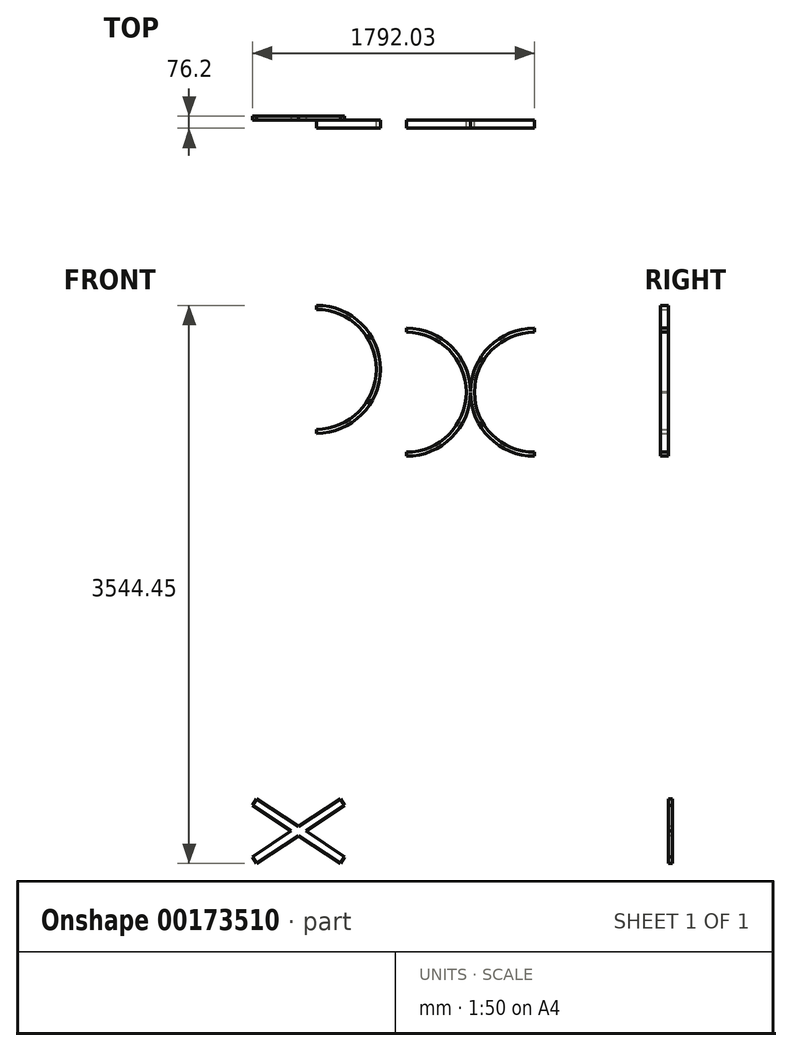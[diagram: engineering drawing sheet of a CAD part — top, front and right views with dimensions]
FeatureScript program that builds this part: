
annotation { "Feature Type Name" : "Feature", "Feature Type Description" : "" }
export const myFeature = defineFeature(function(context is Context, id is Id, definition is map)
    precondition{}
    {
        {
            var Q0;
            Q0=qCreatedBy(makeId("Front.planeOp"),FACE);
            var sketch = newSketch(context, id + "F0", { "sketchPlane" : qUnion([Q0])});
            skLineSegment(sketch, "E0", {"start": v(-517.84, 296.82) * mm, "end": v(548.96, 296.82) * mm, "construction": true});
            skLineSegment(sketch, "E1", {"start": v(15.56, 296.82) * mm, "end": v(15.56, -515.98) * mm, "construction": true});
            skLineSegment(sketch, "E2", {"start": v(421.96, -515.98) * mm, "end": v(904.56, -515.98) * mm});
            skLineSegment(sketch, "E3", {"start": v(904.56, -515.98) * mm, "end": v(421.96, -515.98) * mm});
            skLineSegment(sketch, "E4", {"start": v(15.56, -515.98) * mm, "end": v(15.56, -109.58) * mm, "construction": true});
            skLineSegment(sketch, "E5", {"start": v(15.56, -109.58) * mm, "end": v(-9.84, -109.58) * mm, "construction": true});
            skLineSegment(sketch, "E6", {"start": v(-390.84, 296.84) * mm, "end": v(-390.84, 271.42) * mm});
            skArc(sketch, "E7.MirrorCS", {"start": v(421.96, -515.98) * mm, "mid": v(15.56, -109.58) * mm, "end": v(421.96, 296.82) * mm});
            skLineSegment(sketch, "E8", {"start": v(421.96, 296.82) * mm, "end": v(421.96, 271.42) * mm});
            skArc(sketch, "E9.0", {"start": v(-390.84, -490.58) * mm, "mid": v(-9.84, -109.58) * mm, "end": v(-390.84, 271.42) * mm});
            skArc(sketch, "E10.0", {"start": v(421.96, -490.58) * mm, "mid": v(40.96, -109.58) * mm, "end": v(421.96, 271.42) * mm});
            skLineSegment(sketch, "E11.trimOffspring", {"start": v(-390.84, -490.58) * mm, "end": v(-390.84, -516) * mm});
            skLineSegment(sketch, "E12.trimOffspring", {"start": v(421.96, -490.58) * mm, "end": v(421.96, -515.98) * mm});
            skLineSegment(sketch, "E13.trimOffspring", {"start": v(-390.84, -515.98) * mm, "end": v(-873.44, -515.98) * mm});
            skArc(sketch, "E14.0", {"start": v(-390.84, -516) * mm, "mid": v(-104.6, -398.1) * mm, "end": v(15.57, -112.8) * mm});
            skArc(sketch, "E15.trimOffspring", {"start": v(15.57, -106.37) * mm, "mid": v(-104.6, 178.94) * mm, "end": v(-390.84, 296.84) * mm});
            skLineSegment(sketch, "E16", {"start": v(-390.84, 296.84) * mm, "end": v(421.96, 296.82) * mm});
            skSolve(sketch);
        }
        {
            var Q0;
            {var subQ0=sQuery(id+"F0.wireOp",EDGE,"E6");Q0=makeQuery(id+"F0.imprint","IMPRINT",FACE,{"disambiguationData":[TD([[makeQuery(id+"F0.imprint","IMPRINT",EDGE,{"derivedFrom":subQ0}),1.0]])]});}
            var Q1;
            {var subQ0=sQuery(id+"F0.wireOp",EDGE,"E8");Q1=makeQuery(id+"F0.imprint","IMPRINT",FACE,{"disambiguationData":[TD([[makeQuery(id+"F0.imprint","IMPRINT",EDGE,{"derivedFrom":subQ0}),-1.0]])]});}
            extrude(context, id + "F1", {"entities" : qUnion([Q0, Q1]), "depth" : 50.8 * mm});
        }
        {
            var Q0;
            Q0=qCreatedBy(makeId("Front.planeOp"),FACE);
            var sketch = newSketch(context, id + "F2", { "sketchPlane" : qUnion([Q0])});
            skArc(sketch, "E17", {"start": v(-962.68, -370.57) * mm, "mid": v(-556.28, 35.83) * mm, "end": v(-962.68, 442.23) * mm});
            skLineSegment(sketch, "E18", {"start": v(-962.68, 416.83) * mm, "end": v(-962.68, 442.23) * mm});
            skLineSegment(sketch, "E19", {"start": v(-962.68, 442.23) * mm, "end": v(-962.68, 416.83) * mm});
            skArc(sketch, "E20.0", {"start": v(-962.68, -345.17) * mm, "mid": v(-581.68, 35.83) * mm, "end": v(-962.68, 416.83) * mm});
            skLineSegment(sketch, "E21.trimOffspring", {"start": v(-962.68, -345.17) * mm, "end": v(-962.68, -370.57) * mm});
            skLineSegment(sketch, "E22.bottom", {"start": v(-1889.43, -2364.16) * mm, "end": v(-263.83, -2364.16) * mm});
            skLineSegment(sketch, "E22.top", {"start": v(-1889.43, -3430.96) * mm, "end": v(-263.83, -3430.96) * mm});
            skLineSegment(sketch, "E22.left", {"start": v(-1889.43, -2364.16) * mm, "end": v(-1889.43, -3430.96) * mm});
            skLineSegment(sketch, "E22.right", {"start": v(-263.83, -2364.16) * mm, "end": v(-263.83, -3430.96) * mm});
            skLineSegment(sketch, "E23", {"start": v(-1889.43, -3430.96) * mm, "end": v(-1356.13, -3080.98) * mm});
            skLineSegment(sketch, "E24", {"start": v(-1889.43, -2364.16) * mm, "end": v(-1356.13, -2714.13) * mm});
            skLineSegment(sketch, "E25.0", {"start": v(-1889.43, -2491.16) * mm, "end": v(-263.83, -2491.16) * mm});
            skLineSegment(sketch, "E26.0", {"start": v(-390.83, -2364.16) * mm, "end": v(-390.83, -3430.96) * mm});
            skLineSegment(sketch, "E27", {"start": v(-457.35, -2491.16) * mm, "end": v(-457.35, -2290.36) * mm});
            skLineSegment(sketch, "E28", {"start": v(-457.35, -2491.16) * mm, "end": v(-797.12, -2714.13) * mm});
            skLineSegment(sketch, "E29.0", {"start": v(-1076.63, -2867.18) * mm, "end": v(-1342.2, -2692.9) * mm});
            skLineSegment(sketch, "E29.1", {"start": v(-1076.63, -2867.18) * mm, "end": v(-811.06, -2692.9) * mm});
            skLineSegment(sketch, "E30.0", {"start": v(-1076.63, -2927.94) * mm, "end": v(-1342.2, -3102.22) * mm});
            skLineSegment(sketch, "E30.1", {"start": v(-1076.63, -2927.94) * mm, "end": v(-811.06, -3102.22) * mm});
            skLineSegment(sketch, "E31.0", {"start": v(-1030.34, -2897.56) * mm, "end": v(-783.2, -3059.75) * mm});
            skLineSegment(sketch, "E32", {"start": v(-1370.07, -2735.37) * mm, "end": v(-1342.2, -2692.9) * mm});
            skLineSegment(sketch, "E33", {"start": v(-783.19, -2735.37) * mm, "end": v(-811.06, -2692.9) * mm});
            skLineSegment(sketch, "E34", {"start": v(-783.2, -3059.75) * mm, "end": v(-811.06, -3102.22) * mm});
            skLineSegment(sketch, "E35", {"start": v(-1370.07, -3059.75) * mm, "end": v(-1342.2, -3102.22) * mm});
            skLineSegment(sketch, "E36.trimOffspring", {"start": v(-797.13, -3080.98) * mm, "end": v(-263.83, -3430.96) * mm});
            skLineSegment(sketch, "E37.trimOffspring", {"start": v(-1122.93, -2897.56) * mm, "end": v(-1370.07, -3059.75) * mm});
            skLineSegment(sketch, "E38.trimOffspring", {"start": v(-797.12, -2714.13) * mm, "end": v(-263.83, -2364.16) * mm});
            skLineSegment(sketch, "E39.trimOffspring", {"start": v(-1122.93, -2897.56) * mm, "end": v(-1370.07, -2735.37) * mm});
            skLineSegment(sketch, "E40.trimOffspring", {"start": v(-1030.34, -2897.56) * mm, "end": v(-783.19, -2735.37) * mm});
            skPoint(sketch, "E41.orphan", {"position": v(-1076.63, -2897.56) * mm});
            skSolve(sketch);
        }
        {
            var Q0;
            Q0=makeQuery(id+"F2.imprint","IMPRINT",FACE,{"disambiguationData":[TD([[makeQuery(id+"F2.imprint","IMPRINT",EDGE,{"derivedFrom":sQuery(id+"F2.wireOp",EDGE,"E17")}),1.0]])]});
            extrude(context, id + "F3", {"entities" : qUnion([Q0]), "depth" : 50.8 * mm});
        }
        {
            var Q0;
            {var subQ5=sQuery(id+"F2.wireOp",EDGE,"E29.0");Q0=makeQuery(id+"F2.imprint","IMPRINT",FACE,{"disambiguationData":[TD([[makeQuery(id+"F2.imprint","IMPRINT",EDGE,{"derivedFrom":subQ5}),1.0]])]});}
            extrude(context, id + "F4", {"entities" : qUnion([Q0]), "oppositeDirection" : true, "depth" : 25.4 * mm});
        }
    });
